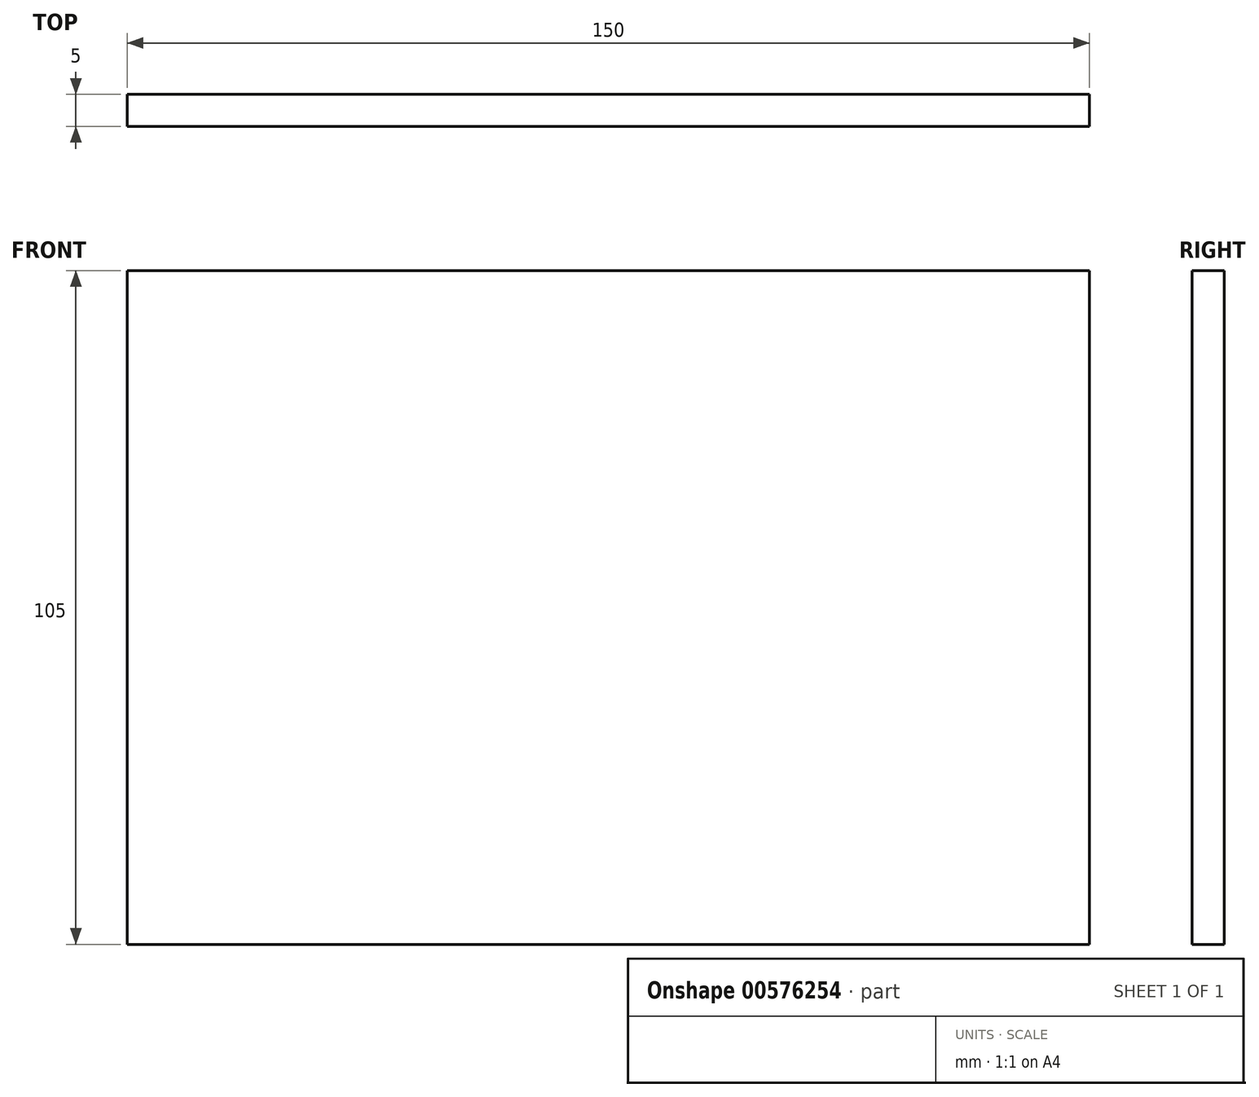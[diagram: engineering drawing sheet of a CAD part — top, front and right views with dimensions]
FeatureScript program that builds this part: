
annotation { "Feature Type Name" : "Feature", "Feature Type Description" : "" }
export const myFeature = defineFeature(function(context is Context, id is Id, definition is map)
    precondition{}
    {
        {
            var Q0;
            Q0=qCreatedBy(makeId("Front.planeOp"),FACE);
            var sketch = newSketch(context, id + "F0", { "sketchPlane" : qUnion([Q0])});
            skLineSegment(sketch, "E0.bottom", {"start": v(75, -52.5) * mm, "end": v(-75, -52.5) * mm});
            skLineSegment(sketch, "E0.top", {"start": v(75, 52.5) * mm, "end": v(-75, 52.5) * mm});
            skLineSegment(sketch, "E0.left", {"start": v(75, -52.5) * mm, "end": v(75, 52.5) * mm});
            skLineSegment(sketch, "E0.right", {"start": v(-75, -52.5) * mm, "end": v(-75, 52.5) * mm});
            skPoint(sketch, "E0.middle", {"position": v(0, 0) * mm});
            skSolve(sketch);
        }
        {
            var Q0;
            Q0 = qSketchRegion(id + "F0", true);
            extrude(context, id + "F1", {"entities" : qUnion([Q0]), "depth" : 5 * mm, "offsetDistance" : 25 * mm});
        }
    });
